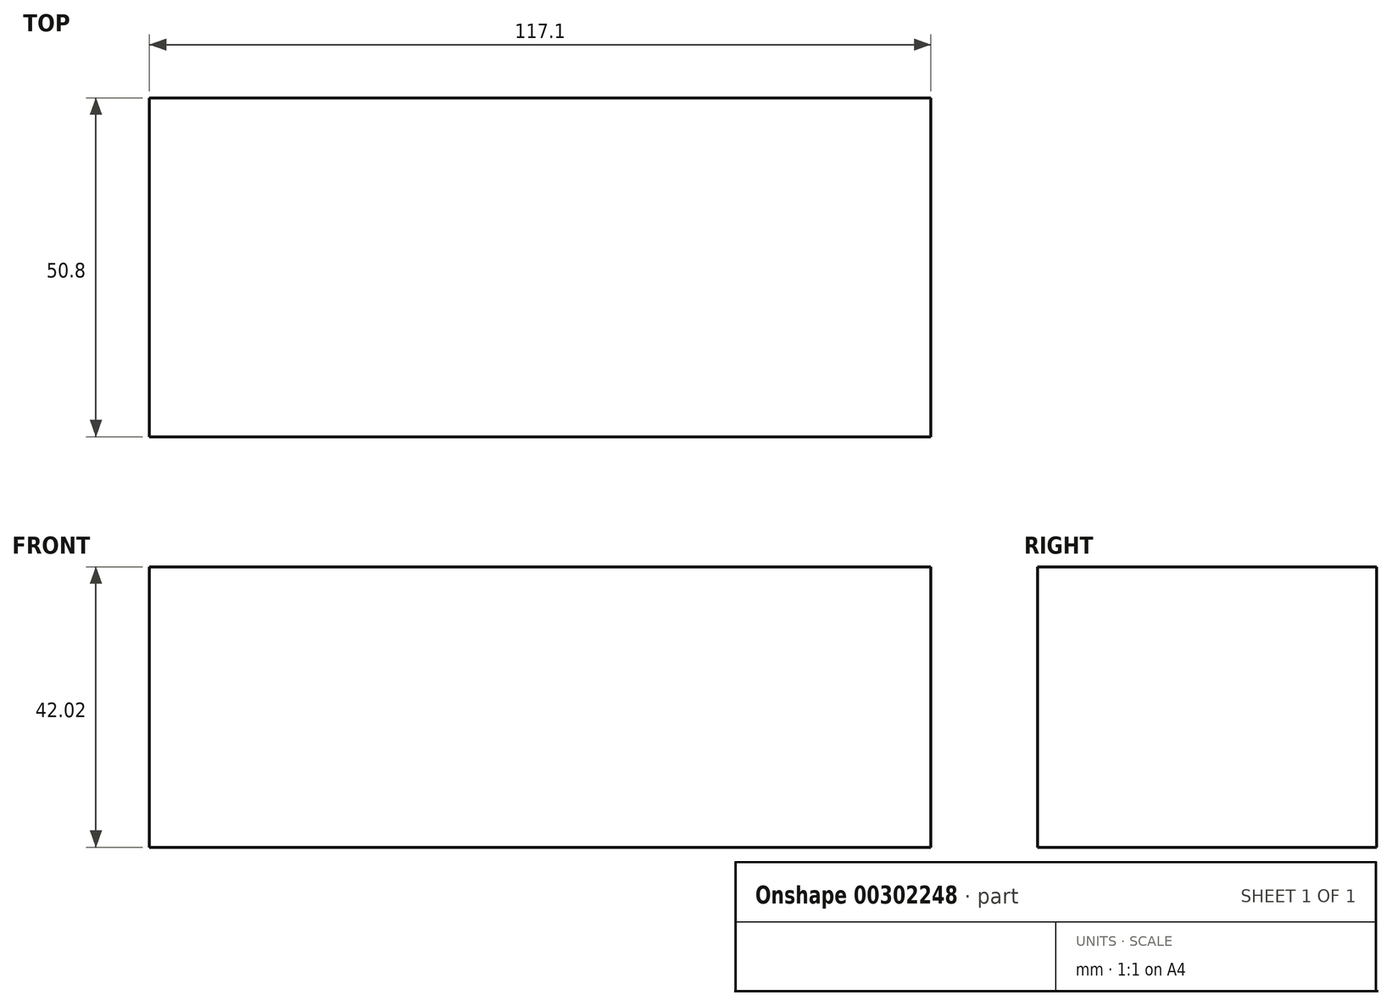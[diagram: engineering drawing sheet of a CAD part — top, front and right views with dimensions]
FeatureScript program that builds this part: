
annotation { "Feature Type Name" : "Feature", "Feature Type Description" : "" }
export const myFeature = defineFeature(function(context is Context, id is Id, definition is map)
    precondition{}
    {
        {
            var Q0;
            Q0=qCreatedBy(makeId("Front.planeOp"),FACE);
            var sketch = newSketch(context, id + "F0", { "sketchPlane" : qUnion([Q0])});
            skLineSegment(sketch, "E0.bottom", {"start": v(-58.55, -21.01) * mm, "end": v(58.55, -21.01) * mm});
            skLineSegment(sketch, "E0.top", {"start": v(-58.55, 21.01) * mm, "end": v(58.55, 21.01) * mm});
            skLineSegment(sketch, "E0.left", {"start": v(-58.55, -21.01) * mm, "end": v(-58.55, 21.01) * mm});
            skLineSegment(sketch, "E0.right", {"start": v(58.55, -21.01) * mm, "end": v(58.55, 21.01) * mm});
            skPoint(sketch, "E0.middle", {"position": v(0, 0) * mm});
            skSolve(sketch);
        }
        {
            var Q0;
            Q0 = qSketchRegion(id + "F0", true);
            extrude(context, id + "F1", {"entities" : qUnion([Q0]), "depth" : 50.8 * mm});
        }
    });
